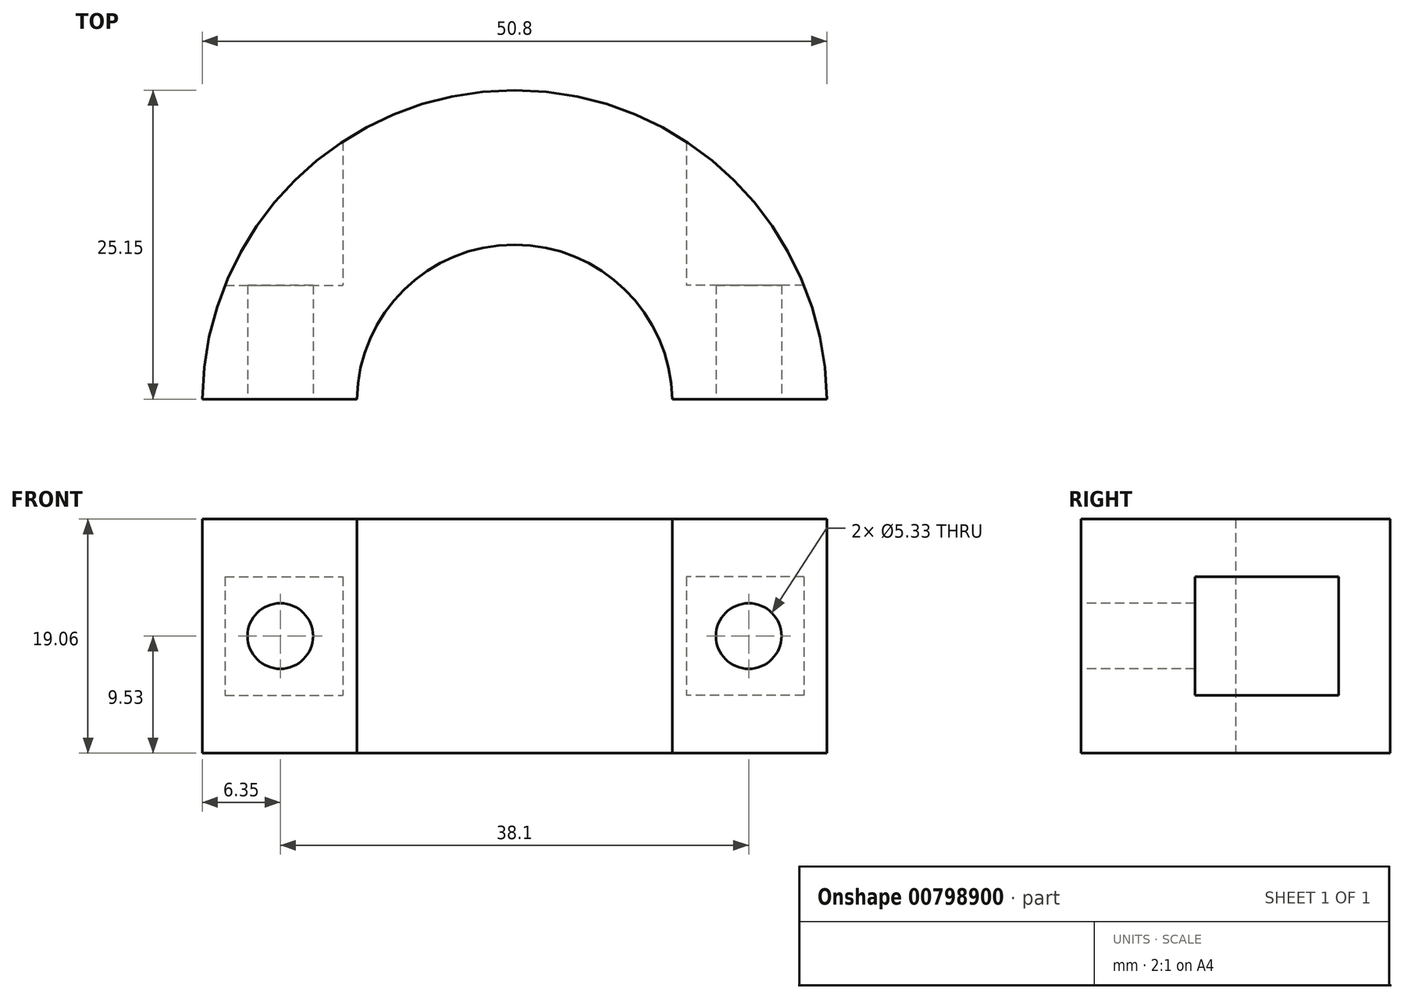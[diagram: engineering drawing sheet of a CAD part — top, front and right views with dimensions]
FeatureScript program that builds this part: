
annotation { "Feature Type Name" : "Feature", "Feature Type Description" : "" }
export const myFeature = defineFeature(function(context is Context, id is Id, definition is map)
    precondition{}
    {
        {
            var Q0;
            Q0=qCreatedBy(makeId("Top.planeOp"),FACE);
            var sketch = newSketch(context, id + "F0", { "sketchPlane" : qUnion([Q0])});
            skArc(sketch, "E0", {"start": v(12.82, 0.25) * mm, "mid": v(0, 12.83) * mm, "end": v(-12.82, 0.25) * mm});
            skArc(sketch, "E1", {"start": v(25.4, 0.25) * mm, "mid": v(0, 25.4) * mm, "end": v(-25.4, 0.25) * mm});
            skLineSegment(sketch, "E2", {"start": v(-25.4, 0.25) * mm, "end": v(-12.82, 0.25) * mm});
            skLineSegment(sketch, "E3.trimOffspring", {"start": v(12.82, 0.25) * mm, "end": v(25.4, 0.25) * mm});
            skSolve(sketch);
        }
        {
            var Q0;
            Q0 = qSketchRegion(id + "F0", true);
            extrude(context, id + "F1", {"entities" : qUnion([Q0]), "endBound" : BoundingType.SYMMETRIC, "depth" : 19.05 * mm, "offsetDistance" : 25.4 * mm});
        }
        {
            var Q0;
            Q0=qCreatedBy(makeId("Front.planeOp"),FACE);
            var sketch = newSketch(context, id + "F2", { "sketchPlane" : qUnion([Q0])});
            skCircle(sketch, "E4", {"center": v(-19.05, 0) * mm, "radius": 2.67 * mm});
            skCircle(sketch, "E5", {"center": v(19.05, 0) * mm, "radius": 2.67 * mm});
            skSolve(sketch);
        }
        {
            var Q0;
            Q0=qCreatedBy(makeId("Front.planeOp"),FACE);
            cPlane(context, id + "F3", {"entities" : qUnion([Q0]), "cplaneType" : CPlaneType.OFFSET, "offset" : 9.52 * mm, "oppositeDirection" : true, "width" : 152.4 * mm, "height" : 152.4 * mm});
        }
        {
            var Q0;
            Q0 = qSketchRegion(id + "F2", true);
            extrude(context, id + "F4", {"entities" : qUnion([Q0]), "operationType" : NewBodyOperationType.REMOVE, "endBound" : BoundingType.THROUGH_ALL, "oppositeDirection" : true, "depth" : 25.4 * mm, "offsetDistance" : 25.4 * mm});
        }
        {
            var Q0;
            Q0=qCreatedBy(id+"F3.planeOp",FACE);
            var sketch = newSketch(context, id + "F5", { "sketchPlane" : qUnion([Q0])});
            skCircle(sketch, "E6.0", {"center": v(19.05, 0) * mm, "radius": 2.67 * mm, "construction": true});
            skCircle(sketch, "E7.0", {"center": v(-19.05, 0) * mm, "radius": 2.67 * mm, "construction": true});
            skLineSegment(sketch, "E8.0", {"start": v(25.4, 9.53) * mm, "end": v(25.4, -9.52) * mm, "construction": true});
            skLineSegment(sketch, "E9.0", {"start": v(-25.4, 9.53) * mm, "end": v(-25.4, -9.52) * mm, "construction": true});
            skLineSegment(sketch, "E10", {"start": v(25.4, 0) * mm, "end": v(-25.4, 0) * mm, "construction": true});
            skLineSegment(sketch, "E11.bottom", {"start": v(25.4, 4.83) * mm, "end": v(13.97, 4.83) * mm});
            skLineSegment(sketch, "E11.top", {"start": v(25.4, -4.83) * mm, "end": v(13.97, -4.83) * mm});
            skLineSegment(sketch, "E11.left", {"start": v(25.4, 4.83) * mm, "end": v(25.4, -4.83) * mm});
            skLineSegment(sketch, "E11.right", {"start": v(13.97, 4.83) * mm, "end": v(13.97, -4.83) * mm});
            skLineSegment(sketch, "E12.bottom", {"start": v(-25.4, 4.83) * mm, "end": v(-13.97, 4.83) * mm});
            skLineSegment(sketch, "E12.top", {"start": v(-25.4, -4.83) * mm, "end": v(-13.97, -4.83) * mm});
            skLineSegment(sketch, "E12.left", {"start": v(-25.4, 4.83) * mm, "end": v(-25.4, -4.83) * mm});
            skLineSegment(sketch, "E12.right", {"start": v(-13.97, 4.83) * mm, "end": v(-13.97, -4.83) * mm});
            skSolve(sketch);
        }
        {
            var Q0;
            Q0 = qSketchRegion(id + "F5", true);
            extrude(context, id + "F6", {"entities" : qUnion([Q0]), "operationType" : NewBodyOperationType.REMOVE, "endBound" : BoundingType.THROUGH_ALL, "oppositeDirection" : true, "depth" : 25.4 * mm, "offsetDistance" : 25.4 * mm});
        }
    });
